# Revit family: Accessory-Toilet_Brush_Holder-KOHLER-Loure-K-11746T
name_source: partatom
category: Specialty Equipment
units: mm (PartAtom-declared; Revit-internal decimal feet)

## family parameters
Cut with Voids When Loaded = No
Host = Face
OmniClass Number = 23.31.25.00
OmniClass Title = Toilet and Bath Specialties
Part Type = Normal
Room Calculation Point = No
Round Connector Dimension = Use Diameter
Shared = No

## types (3) — shared parameters
ADA Compliant = No
Assembly Code = C1030200
Date Modified = 11/18/2022
Default Elevation = 42"
Description = Toilet Brush Holder
Height = 14 7/16"
Length = 3 5/16"
Manufacturer = Kohler Co.
Master Format 2014 = 10 28 00
Master Format 2014 Name = Toilet, Bath, and Laundry Accessories
Material = Premium Metal Construction
Product Documentation Link = https://files.kohler.com.cn
Product Name = Loure
URL = http://www.kohler.com.cn
WaterSense Certified = No
Width = 3 1/8"

## per-type parameters (varying)
| type | Finish | Model | Product Page URL | Type |
| BL-Matte Black | Kohler-Metal-BL-Matte_Black | K-11746T-BL |  | 1 |
| BV-Brushed Bronze | Kohler-Metal-BV-Brushed_Bronze | K-11746T-BV |  | 2 |
| CP-Polished Chrome | Kohler-Metal-CP-Polished_Chrome | K-11746T-CP | https://www.kohler.com.cn | 3 |

## geometry (parser evidence)
native form markers: Sweep x4
no freeform markers — native parametric forms only
